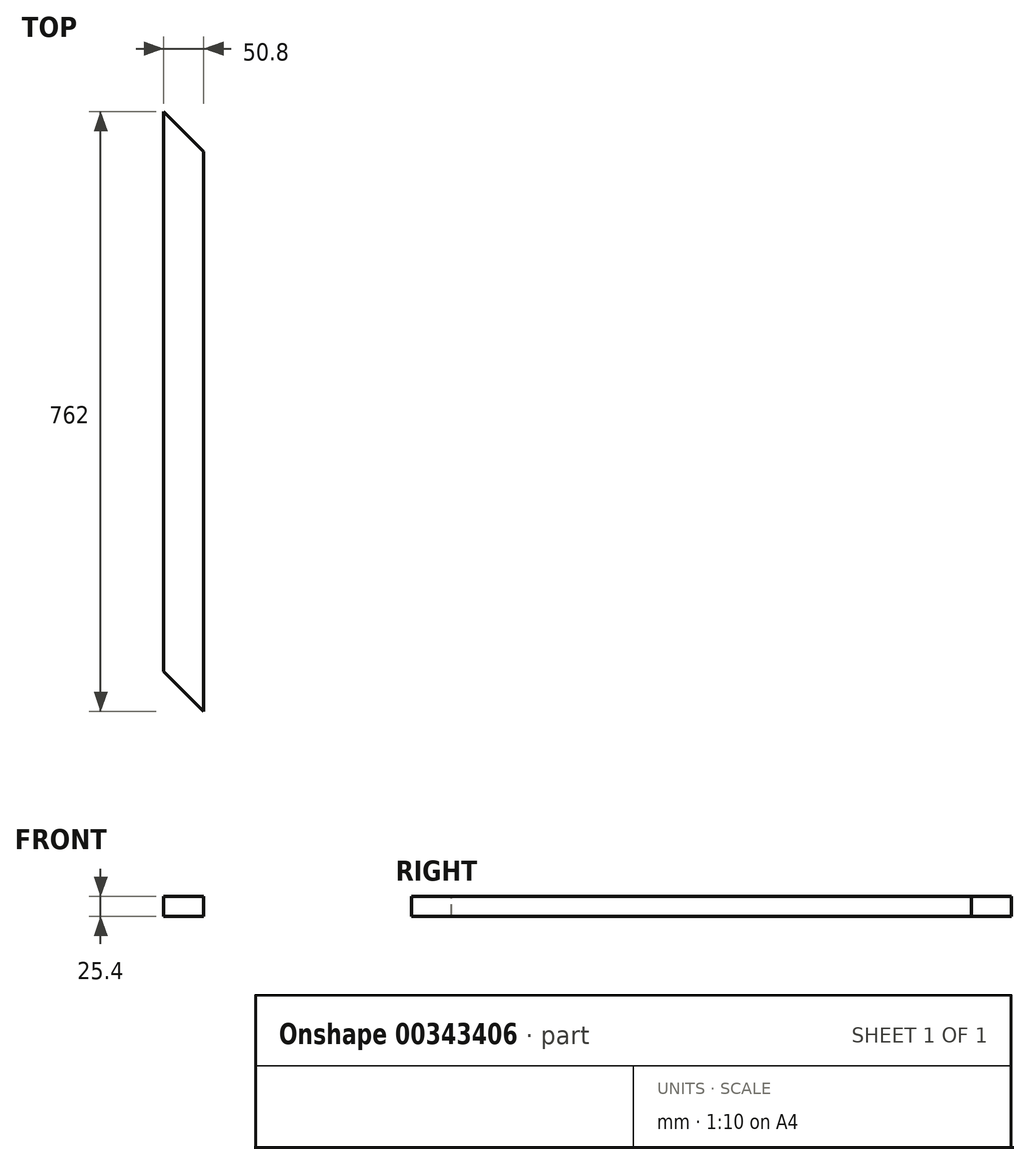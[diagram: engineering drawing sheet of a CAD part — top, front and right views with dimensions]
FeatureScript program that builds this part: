
annotation { "Feature Type Name" : "Feature", "Feature Type Description" : "" }
export const myFeature = defineFeature(function(context is Context, id is Id, definition is map)
    precondition{}
    {
        {
            var Q0;
            Q0=qCreatedBy(makeId("Front.planeOp"),FACE);
            var sketch = newSketch(context, id + "F0", { "sketchPlane" : qUnion([Q0])});
            skLineSegment(sketch, "E0.bottom", {"start": v(-4.93, 6.4) * mm, "end": v(-55.73, 6.4) * mm});
            skLineSegment(sketch, "E0.top", {"start": v(-4.93, 31.8) * mm, "end": v(-55.73, 31.8) * mm});
            skLineSegment(sketch, "E0.left", {"start": v(-4.93, 6.4) * mm, "end": v(-4.93, 31.8) * mm});
            skLineSegment(sketch, "E0.right", {"start": v(-55.73, 6.4) * mm, "end": v(-55.73, 31.8) * mm});
            skSolve(sketch);
        }
        {
            var Q0;
            Q0 = qSketchRegion(id + "F0", true);
            extrude(context, id + "F1", {"entities" : qUnion([Q0]), "depth" : 762 * mm});
        }
        {
            var Q0;
            Q0=makeQuery(id+"F1.opExtrude","CAP_EDGE",EDGE,{"disambiguationData":[OSD([sQuery(id+"F0.wireOp",EDGE,"E0.right")])],"isStart":false});
            chamfer(context, id + "F2", {"entities" : qUnion([Q0]), "width" : 50.8 * mm, "tangentPropagation" : true});
        }
        {
            var Q0;
            Q0=makeQuery(id+"F1.opExtrude","CAP_EDGE",EDGE,{"disambiguationData":[OSD([sQuery(id+"F0.wireOp",EDGE,"E0.left")])],"isStart":true});
            chamfer(context, id + "F3", {"entities" : qUnion([Q0]), "width" : 50.8 * mm, "tangentPropagation" : true});
        }
    });
